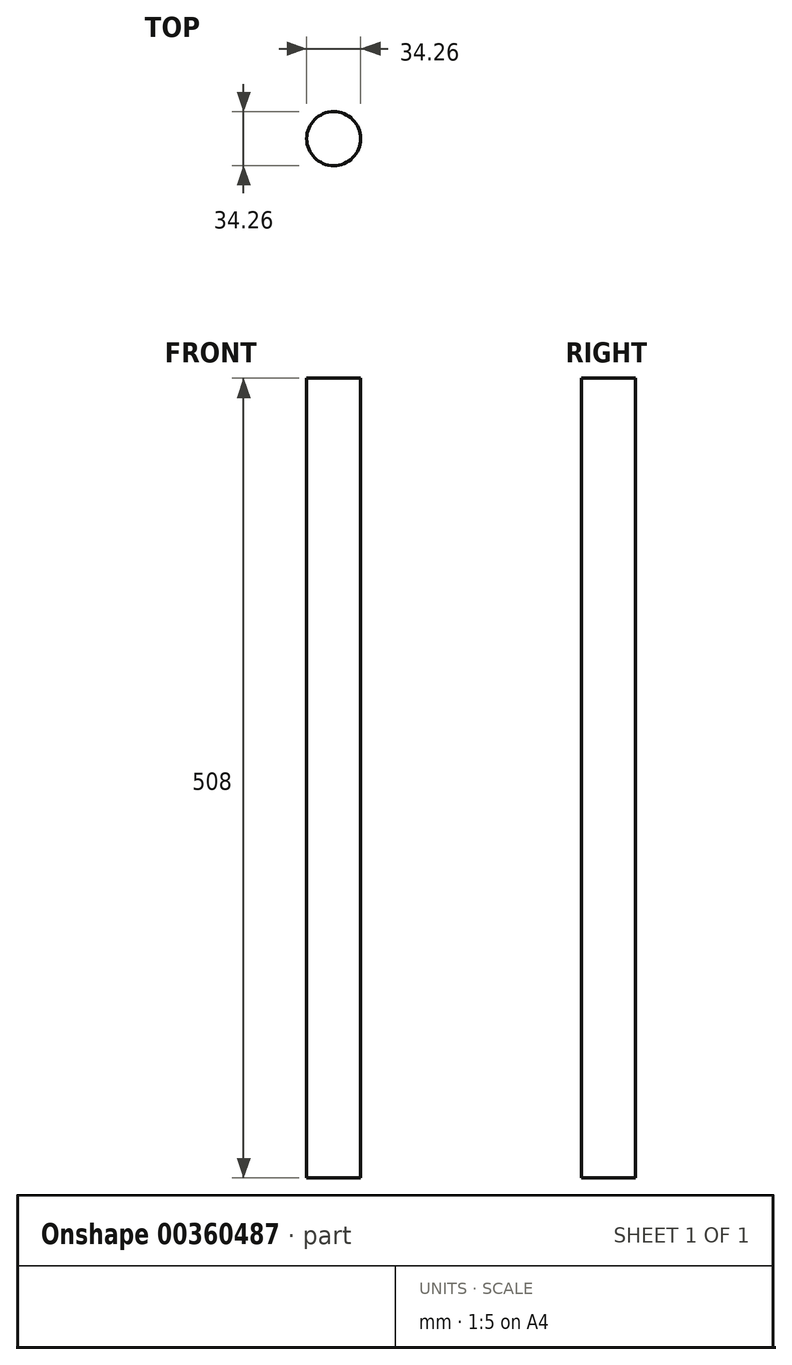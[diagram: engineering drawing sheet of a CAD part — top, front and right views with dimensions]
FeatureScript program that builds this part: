
annotation { "Feature Type Name" : "Feature", "Feature Type Description" : "" }
export const myFeature = defineFeature(function(context is Context, id is Id, definition is map)
    precondition{}
    {
        {
            var Q0;
            Q0=qCreatedBy(makeId("Top.planeOp"),FACE);
            var sketch = newSketch(context, id + "F0", { "sketchPlane" : qUnion([Q0])});
            skCircle(sketch, "E0", {"center": v(0, 0) * mm, "radius": 17.13 * mm});
            skSolve(sketch);
        }
        {
            var Q0;
            Q0=makeQuery(id+"F0.imprint","IMPRINT",FACE,{"disambiguationData":[TD([[makeQuery(id+"F0.imprint","IMPRINT",EDGE,{"derivedFrom":sQuery(id+"F0.wireOp",EDGE,"E0")}),1.0]])]});
            extrude(context, id + "F1", {"entities" : qUnion([Q0]), "depth" : 508 * mm});
        }
    });
